# Revit family: 1354887957SUPAflo_SF62_LOD200
name_source: partatom
category: Mechanical Equipment
revit_build: Autodesk Revit 2014 (Build: 20130308_1515(x64)
units: mm (PartAtom-declared; Revit-internal decimal feet)

## types (1)
- SF62
    Access Clearance Bottom = 0.000 mm
    Access Clearance Front = 800.000 mm
    Access Clearance Left = 450.000 mm
    Access Clearance Rear = 450.000 mm
    Access Clearance Right = 450.000 mm
    Access Clearance Top = 450.000 mm
    Air Inlet Connection Size = 130.000 mm
    Air Intake Connector = Air Intake Connection
    Air Supply = Yes
    Annually = As per attached URL O & M Manual
    Assembly Code = D3020100
    BMS Links = Yes
    Burner Control Type = Modulating
    CE Approval = Yes - 0063BS3840
    Clean Out and Inspection Opening Type = Other
    Clearence Box = Glass - Clear - Amber
    Colour = Blue (RAL 5011) & White (RAL 9016)
    Condensate Drain Size = 22.000 mm
    Condensate Drain Type = Plain
    Configuration = Single Boiler
    Continuous Output at 44 Degree Differential l/h = 3700
    Continuous Output at 50 Degree Differential l/h = 3240
    Control Options = Modulating
    Control Thermostat Range Note = 40°C - 75°C
    Control ThermostatRange = 40 °C
    Control Type = Internal
    Default Elevation = 0.000 mm
    Description = Condensing Boiler
    Drain Connection Size = 0.000 mm
    Drain Connection Type = Other
    External Material = Steel
    Features = Premix Forced Draught Condensing Water Heaterr
    Finish = Powder Coated Steel
    Flow and Return Connection Size = 50.800 mm
    Flow and Return Connection Type = Threaded
    Flue Connection Standard = 150mm
    Flue Connection Type = Socket
    Flue or Air Intake Classification = B23, C33, C43, C53, C63 & C83
    Frequency = 50 Hz
    Fuel Connection Size = 25.400 mm
    Fuel Type = Gas - NG
    Full Load Current = 10 A
    Fuse Rating = 200 A
    Gas Connection Pipe Diameter = 19.000 mm
    Gas Consumption rate = 18 m³/h
    Gross Input = 194 kW
    Gross Weight = 295.00 kg
    Heat Exchanger Material = Stainless Steel
    Heat Generator Efficiency = 98%
    Heat Generator Thermal Efficiency = 106%
    Heat Up Time mins = 1
    Heater Operation = Fully Condensing
    Heating Circuit Flow Diameter = 32.000 mm
    IK Rating = 1.75
    IP Rating = 20
    Instrument Box Panel = Metal - Polished Silver
    Insulation Thickness = 0.000 mm
    Insulation Type = Integral Thermal Insulation
    Interlocks = Yes
    Manufacturer = Andrews Water Heaters
    Max Operating Pressure When Open Vented = 6.00 bar
    Max Operating Pressure When Unvented = 3.50 bar
    Maximum Gas Inlet Pressure mbar = 50
    Maximum Oil Inlet Pressure mbar = 0
    Maximum Power Consumption = 35 W
    Maximum Water Temperature = 75 °C
    Min Operating Pressure = 1.00 bar
    Minimum Gas Inlet Pressure mbar = 18
    Minimum Oil Inlet Pressure mbar = 0
    Minimum Power Consumption = 380 W
    Model = SF62
    Mounting = Floor Standing
    NOx Emissions mg = 35 kWh
    Nominal Gas Inlet Pressure = 21 mbar
    Nominal Oil Inlet Pressure mbar = 0
    O&M Manual = http://www.andrewswaterheaters.co.uk
    Product Literature = http://www.andrewswaterheaters.co.uk
    Product Model Number = 1011037
    Product Range = SUPAflo Range
    Rated Criteria = 80/60
    Rated Output kW = 61
    Recovery Rate litre/min = 54
    Reference Standard = BSE 26
    Safety Valve Connection Size = 0.000 mm
    Safety Valve Connection Type = Other
    Secondary Return Connection Size = 0.000 mm
    Secondary Return Connection Type = Other
    Shape = Rectangular (Horizontal)
    Shipping Weight = 360.00 kg
    Siphon Bush Pipe Diameter = 19.000 mm
    Sound Pressure Level dBA = 59
    Standing Loss W = 0.18
    Starting Current = 2 A
    Supply Phase = Single Phase
    Text Material = Paint - Black
    Type = Direct Gas Fired Instaneous Water Heater
    URL = http://www.andrewswaterheaters.co.uk
    Voltage = 230 V
    WRAS Approval = 1011037
    Water Content = 31.00 L
    Water Treatment Required = Yes

## geometry (parser evidence)
native form markers: Blend x74, Sweep x2
no freeform markers — native parametric forms only
